# Revit family: Flooring_Entrance-Flooring_emco_DIPLOMAT-Premium
name_source: partatom
category: Furniture Systems
revit_build: Autodesk Revit 2018 (Build: 20190510_1515(x64)
units: mm (PartAtom-declared; Revit-internal decimal feet)

## family parameters
Cut with Voids When Loaded = No
Host = Face
OmniClass Number = 23.15.17.11.11
OmniClass Title = Floor Toppings
Part Type = Normal
Room Calculation Point = No
Round Connector Dimension = Use Diameter
Shared = No

## types (99) — shared parameters
Assembly Code = E2010400
Date Updated = 2023/08/22
Default Elevation = 1219 mm
Description = Rollable and hard-wearing original entrance mat with standard insert for supported installation options.
Keynote = 12480.A1
Manufacturer = Emco
Product data url = https://bimobject.com
Profile Material = Emco - Metal - Aluminium
Standard profile clearance approx. (mm) = 5 mm, rubber spacers
URL = https://www.emco-bau.com
Version = 1

## per-type parameters (varying)
| type | Brush strip | Colour fastness to artificial light ISO 105-B02 | Colour fastness to rubbing ISO 105 X12 | Colour fastness to water ISO 105 E01 | EPIMID | Flammability | Height 12 | Height 17 | Height 22 | Large | Normal | Pile material | Profile width (mm) | Scraping edge | Slip resistance | Tread surface | Weight (kg/m2) | z_Height | z_edge_height | z_insert_offset | z_insert_width | z_slot_offest | z_slot_width |
| Large With Care insert 512 PL Care | No | good 5-6 | good 4-5 | good 4-5 | 99836 | Fire classification for the complete mat system Cfl-s1 in accordance with EN 13501 | Yes | No | No | Yes | No | 100% PA 6 (polyamide) | 44 mm | No | R 12 slip resistance as per DIN 51130 | The robust and exceptionally abrasion-resistant Care insert for the effective reduction of fine dirt. | 8.9 | 12 mm  [stored 0.0393701 ft] | 16 mm | 49 mm | 44 mm  [stored 0.144357 ft] | 47 mm | 5 mm  [stored 0.0164042 ft] |
| Large With Care insert 517 PL Care | No | good 5-6 | good 4-5 | good 4-5 | 99838 | Fire classification for the complete mat system Cfl-s1 in accordance with EN 13501 | No | Yes | No | Yes | No | 100% PA 6 (polyamide) | 44 mm | No | R 12 slip resistance as per DIN 51130 | The robust and exceptionally abrasion-resistant Care insert for the effective reduction of fine dirt. | 95 | 17 mm | 20 mm  [stored 0.0656168 ft] | 49 mm | 44 mm  [stored 0.144357 ft] | 47 mm | 5 mm  [stored 0.0164042 ft] |
| Large With Care insert 522 PL Care | No | good 5-6 | good 4-5 | good 4-5 | 99840 | Fire classification for the complete mat system Cfl-s1 in accordance with EN 13501 | No | No | Yes | Yes | No | 100% PA 6 (polyamide) | 44 mm | No | R 12 slip resistance as per DIN 51130 | The robust and exceptionally abrasion-resistant Care insert for the effective reduction of fine dirt. | 10.5 | 22 mm  [stored 0.0721785 ft] | 25 mm  [stored 0.082021 ft] | 49 mm | 44 mm  [stored 0.144357 ft] | 47 mm | 5 mm  [stored 0.0164042 ft] |
| Large With Care insert and brush strip 517 PL Care B | Yes | good 5-6 | good 4-5 | good 4-5 | 104455 | Insert with fire classification Cfl-s1 according to EN 13501. | No | Yes | No | Yes | No | 100% PA 6 (polyamide) | 44 mm | No | - | The robust and exceptionally abrasion-resistant Care insert for the effective reduction of fine dirt. The additional profile increases the cleaning power. | 9.6 | 17 mm | 20 mm  [stored 0.0656168 ft] | 64 mm | 44 mm  [stored 0.144357 ft] | 54 mm | 20 mm  [stored 0.0656168 ft] |
| Large With Care insert and brush strip 522 PL Care B | Yes | good 5-6 | good 4-5 | good 4-5 | 104456 | Insert with fire classification Cfl-s1 according to EN 13501. | No | No | Yes | Yes | No | 100% PA 6 (polyamide) | 44 mm | No | - | The robust and exceptionally abrasion-resistant Care insert for the effective reduction of fine dirt. The additional profile increases the cleaning power. | 10.7 | 22 mm  [stored 0.0721785 ft] | 25 mm  [stored 0.082021 ft] | 64 mm | 44 mm  [stored 0.144357 ft] | 54 mm | 20 mm  [stored 0.0656168 ft] |
| Large With Care insert and scraping edge 512 PL Care K | No | good 5-6 | good 4-5 | good 4-5 | 104450 | Insert with fire classification Cfl-s1 according to EN 13501. | Yes | No | No | Yes | No | 100% PA 6 (polyamide) | 44 mm | Yes | - | The robust and exceptionally abrasion-resistant Care insert for the effective reduction of fine dirt. The additional profile increases the cleaning power. | 9.2 | 12 mm  [stored 0.0393701 ft] | 16 mm | 59 mm | 44 mm  [stored 0.144357 ft] | 52 mm | 15 mm  [stored 0.0492126 ft] |
| Large With Care insert and scraping edge 517 PL Care K | No | good 5-6 | good 4-5 | good 4-5 | 104451 | Insert with fire classification Cfl-s1 according to EN 13501. | No | Yes | No | Yes | No | 100% PA 6 (polyamide) | 44 mm | Yes | - | The robust and exceptionally abrasion-resistant Care insert for the effective reduction of fine dirt. The additional profile increases the cleaning power. | 13.5 | 17 mm | 20 mm  [stored 0.0656168 ft] | 59 mm | 44 mm  [stored 0.144357 ft] | 52 mm | 15 mm  [stored 0.0492126 ft] |
| Large With Care insert and scraping edge 522 PL Care K | No | good 5-6 | good 4-5 | good 4-5 | 104452 | Insert with fire classification Cfl-s1 according to EN 13501. | No | No | Yes | Yes | No | 100% PA 6 (polyamide) | 44 mm | Yes | - | The robust and exceptionally abrasion-resistant Care insert for the effective reduction of fine dirt. The additional profile increases the cleaning power. | 12 | 22 mm  [stored 0.0721785 ft] | 25 mm  [stored 0.082021 ft] | 59 mm | 44 mm  [stored 0.144357 ft] | 52 mm | 15 mm  [stored 0.0492126 ft] |
| Large With Conform insert 512 PL Conform | No | - | - | - | 99859 | Fire classification for the complete mat system Cfl-s1 in accordance with EN 13501 | Yes | No | No | Yes | No | 100% PA 6 (polyamide) | 44 mm | No | R 12 slip resistance as per DIN 51130 | The Conform insert made of recycled materials is the perfect complement to wooden surroundings and can be used in a whole host of environments. | 9.1 | 12 mm  [stored 0.0393701 ft] | 16 mm | 49 mm | 44 mm  [stored 0.144357 ft] | 47 mm | 5 mm  [stored 0.0164042 ft] |
| Large With Conform insert 517 PL Conform | No | - | - | - | 99863 | Fire classification for the complete mat system Cfl-s1 in accordance with EN 13501 | No | Yes | No | Yes | No | 100% PA 6 (polyamide) | 44 mm | No | R 12 slip resistance as per DIN 51130 | The Conform insert made of recycled materials is the perfect complement to wooden surroundings and can be used in a whole host of environments. | 9.6 | 17 mm | 20 mm  [stored 0.0656168 ft] | 49 mm | 44 mm  [stored 0.144357 ft] | 47 mm | 5 mm  [stored 0.0164042 ft] |
| Large With Conform insert 522 PL Conform | No | - | - | - | 99867 | Fire classification for the complete mat system Cfl-s1 in accordance with EN 13501 | No | No | Yes | Yes | No | 100% PA 6 (polyamide) | 44 mm | No | R 12 slip resistance as per DIN 51130 | The Conform insert made of recycled materials is the perfect complement to wooden surroundings and can be used in a whole host of environments. | 10.6 | 22 mm  [stored 0.0721785 ft] | 25 mm  [stored 0.082021 ft] | 49 mm | 44 mm  [stored 0.144357 ft] | 47 mm | 5 mm  [stored 0.0164042 ft] |
| Large With Conform insert and brush strip 517 PL Conform B | Yes | - | - | - | 105730 | Insert with fire classification Cfl-s1 according to EN 13501. | No | Yes | No | Yes | No | 100% PA 6 (polyamide) | 44 mm | No | - | The Conform insert made of recycled materials is the perfect complement to wooden surroundings and can be used in a whole host of environments. The additional profile increases the cleaning power. | 97 | 17 mm | 20 mm  [stored 0.0656168 ft] | 64 mm | 44 mm  [stored 0.144357 ft] | 54 mm | 20 mm  [stored 0.0656168 ft] |
| Large With Conform insert and brush strip 522 PL Conform B | Yes | - | - | - | 105731 | Insert with fire classification Cfl-s1 according to EN 13501. | No | No | Yes | Yes | No | 100% PA 6 (polyamide) | 44 mm | No | - | The Conform insert made of recycled materials is the perfect complement to wooden surroundings and can be used in a whole host of environments. The additional profile increases the cleaning power. | 10.8 | 22 mm  [stored 0.0721785 ft] | 25 mm  [stored 0.082021 ft] | 64 mm | 44 mm  [stored 0.144357 ft] | 54 mm | 20 mm  [stored 0.0656168 ft] |
| Large With Conform insert and scraping edge 512 PL Conform K | No | - | - | - | 105724 | Insert with fire classification Cfl-s1 according to EN 13501. | Yes | No | No | Yes | No | 100% PA 6 (polyamide) | 44 mm | Yes | - | The Conform insert made of recycled materials is the perfect complement to wooden surroundings and can be used in a whole host of environments. The additional profile increases the cleaning power. | 93 | 12 mm  [stored 0.0393701 ft] | 16 mm | 59 mm | 44 mm  [stored 0.144357 ft] | 52 mm | 15 mm  [stored 0.0492126 ft] |
| Large With Conform insert and scraping edge 517 PL Conform K | No | - | - | - | 105725 | Insert with fire classification Cfl-s1 according to EN 13501. | No | Yes | No | Yes | No | 100% PA 6 (polyamide) | 44 mm | Yes | - | The Conform insert made of recycled materials is the perfect complement to wooden surroundings and can be used in a whole host of environments. The additional profile increases the cleaning power. | 10.6 | 17 mm | 20 mm  [stored 0.0656168 ft] | 59 mm | 44 mm  [stored 0.144357 ft] | 52 mm | 15 mm  [stored 0.0492126 ft] |
| Large With Conform insert and scraping edge 522 PL Conform K | No | - | - | - | 105726 | Insert with fire classification Cfl-s1 according to EN 13501. | No | No | Yes | Yes | No | 100% PA 6 (polyamide) | 44 mm | Yes | - | The Conform insert made of recycled materials is the perfect complement to wooden surroundings and can be used in a whole host of environments. The additional profile increases the cleaning power. | 12.2 | 22 mm  [stored 0.0721785 ft] | 25 mm  [stored 0.082021 ft] | 59 mm | 44 mm  [stored 0.144357 ft] | 52 mm | 15 mm  [stored 0.0492126 ft] |
| Large With Innova insert 512 PL Innova | No | good 5-6 | good 4-5 | good 4-5 | 99843 | Fire classification for the complete mat system Cfl-s1 in accordance with EN 13501 | Yes | No | No | Yes | No | 100% PA 6 (polyamide) | 44 mm | No | R 12 slip resistance as per DIN 51130 | The exceptionally flexible Innova insert not only creates a sophisticated impression but also improves room acoustics. | 87 | 12 mm  [stored 0.0393701 ft] | 16 mm | 49 mm | 44 mm  [stored 0.144357 ft] | 47 mm | 5 mm  [stored 0.0164042 ft] |
| Large With Innova insert 517 PL Innova | No | good 5-6 | good 4-5 | good 4-5 | 99845 | Fire classification for the complete mat system Cfl-s1 in accordance with EN 13501 | No | Yes | No | Yes | No | 100% PA 6 (polyamide) | 44 mm | No | R 12 slip resistance as per DIN 51130 | The exceptionally flexible Innova insert not only creates a sophisticated impression but also improves room acoustics. | 93 | 17 mm | 20 mm  [stored 0.0656168 ft] | 49 mm | 44 mm  [stored 0.144357 ft] | 47 mm | 5 mm  [stored 0.0164042 ft] |
| Large With Innova insert 522 PL Innova | No | good 5-6 | good 4-5 | good 4-5 | 99847 | Fire classification for the complete mat system Cfl-s1 in accordance with EN 13501 | No | No | Yes | Yes | No | 100% PA 6 (polyamide) | 44 mm | No | R 12 slip resistance as per DIN 51130 | The exceptionally flexible Innova insert not only creates a sophisticated impression but also improves room acoustics. | 10.2 | 22 mm  [stored 0.0721785 ft] | 25 mm  [stored 0.082021 ft] | 49 mm | 44 mm  [stored 0.144357 ft] | 47 mm | 5 mm  [stored 0.0164042 ft] |
| Large With Innova insert and brush strip 517 PL Innova B | Yes | good 5-6 | good 4-5 | good 4-5 | 105740 | Insert with fire classification Cfl-s1 according to EN 13501. | No | Yes | No | Yes | No | 100% PA 6 (polyamide) | 44 mm | No | - | The exceptionally flexible Innova insert not only creates a sophisticated impression but also improves room acoustics. The additional profile increases the cleaning power. | 9.4 | 17 mm | 20 mm  [stored 0.0656168 ft] | 64 mm | 44 mm  [stored 0.144357 ft] | 54 mm | 20 mm  [stored 0.0656168 ft] |
| Large With Innova insert and brush strip 522 PL Innova B | Yes | good 5-6 | good 4-5 | good 4-5 | 105741 | Insert with fire classification Cfl-s1 according to EN 13501. | No | No | Yes | Yes | No | 100% PA 6 (polyamide) | 44 mm | No | - | The exceptionally flexible Innova insert not only creates a sophisticated impression but also improves room acoustics. The additional profile increases the cleaning power. | 10.5 | 22 mm  [stored 0.0721785 ft] | 25 mm  [stored 0.082021 ft] | 64 mm | 44 mm  [stored 0.144357 ft] | 54 mm | 20 mm  [stored 0.0656168 ft] |
| Large With Innova insert and scraping edge 512 PL Innova K | No | good 5-6 | good 4-5 | good 4-5 | 105737 | Insert with fire classification Cfl-s1 according to EN 13501. | Yes | No | No | Yes | No | 100% PA 6 (polyamide) | 44 mm | Yes | - | The exceptionally flexible Innova insert not only creates a sophisticated impression but also improves room acoustics. The additional profile increases the cleaning power. | 8.9 | 12 mm  [stored 0.0393701 ft] | 16 mm | 59 mm | 44 mm  [stored 0.144357 ft] | 52 mm | 15 mm  [stored 0.0492126 ft] |
| Large With Innova insert and scraping edge 517 PL Innova K | No | good 5-6 | good 4-5 | good 4-5 | 105738 | Insert with fire classification Cfl-s1 according to EN 13501. | No | Yes | No | Yes | No | 100% PA 6 (polyamide) | 44 mm | Yes | - | The exceptionally flexible Innova insert not only creates a sophisticated impression but also improves room acoustics. The additional profile increases the cleaning power. | 10.3 | 17 mm | 20 mm  [stored 0.0656168 ft] | 59 mm | 44 mm  [stored 0.144357 ft] | 52 mm | 15 mm  [stored 0.0492126 ft] |
| Large With Innova insert and scraping edge 522 PL Innova K | No | good 5-6 | good 4-5 | good 4-5 | 105739 | Insert with fire classification Cfl-s1 according to EN 13501. | No | No | Yes | Yes | No | 100% PA 6 (polyamide) | 44 mm | Yes | - | The exceptionally flexible Innova insert not only creates a sophisticated impression but also improves room acoustics. The additional profile increases the cleaning power. | 119 | 22 mm  [stored 0.0721785 ft] | 25 mm  [stored 0.082021 ft] | 59 mm | 44 mm  [stored 0.144357 ft] | 52 mm | 15 mm  [stored 0.0492126 ft] |
| Large With Maximus Image insert 512 PL Maximus Image | No | good 5-6 | good 5 | good 5 | 100670 | Fire classification for the complete mat system Bfl-s1 in accordance with EN 13501 | Yes | No | No | Yes | No | 100% PA 6.6 (polyamide) | 44 mm | No | R 12 slip resistance as per DIN 51130 | The Maximus Image insert is suitable for single-colour printing in a personally chosen colour. | 8.9 | 12 mm  [stored 0.0393701 ft] | 16 mm | 49 mm | 44 mm  [stored 0.144357 ft] | 47 mm | 5 mm  [stored 0.0164042 ft] |
| Large With Maximus Image insert 512 PL Maximus Image + Design | No | good 5-6 | good 5 | good 5 | 100669 | Fire classification for the complete mat system Bfl-s1 in accordance with EN 13501 | Yes | No | No | Yes | No | 100% PA 6.6 (polyamide) | 44 mm | No | R 12 slip resistance as per DIN 51130 | The Maximus Image insert is suitable for single-colour printing of logos and lettering. | 8.9 | 12 mm  [stored 0.0393701 ft] | 16 mm | 49 mm | 44 mm  [stored 0.144357 ft] | 47 mm | 5 mm  [stored 0.0164042 ft] |
| Large With Maximus Image insert 517 PL Maximus Image | No | good 5-6 | good 5 | good 5 | 100671 | Fire classification for the complete mat system Bfl-s1 in accordance with EN 13501 | No | Yes | No | Yes | No | 100% PA 6.6 (polyamide) | 44 mm | No | R 12 slip resistance as per DIN 51130 | The Maximus Image insert is suitable for single-colour printing in a personally chosen colour. | 95 | 17 mm | 20 mm  [stored 0.0656168 ft] | 49 mm | 44 mm  [stored 0.144357 ft] | 47 mm | 5 mm  [stored 0.0164042 ft] |
| Large With Maximus Image insert 517 PL Maximus Image + Design | No | good 5-6 | good 5 | good 5 | 100668 | Fire classification for the complete mat system Bfl-s1 in accordance with EN 13501 | No | Yes | No | Yes | No | 100% PA 6.6 (polyamide) | 44 mm | No | R 12 slip resistance as per DIN 51130 | The Maximus Image insert is suitable for single-colour printing of logos and lettering. | 95 | 17 mm | 20 mm  [stored 0.0656168 ft] | 49 mm | 44 mm  [stored 0.144357 ft] | 47 mm | 5 mm  [stored 0.0164042 ft] |
| Large With Maximus Image insert 522 PL Maximus Image | No | good 5-6 | good 5 | good 5 | 100672 | Fire classification for the complete mat system Bfl-s1 in accordance with EN 13501 | No | No | Yes | Yes | No | 100% PA 6.6 (polyamide) | 44 mm | No | R 12 slip resistance as per DIN 51130 | The Maximus Image insert is suitable for single-colour printing in a personally chosen colour. | 0 | 22 mm  [stored 0.0721785 ft] | 25 mm  [stored 0.082021 ft] | 49 mm | 44 mm  [stored 0.144357 ft] | 47 mm | 5 mm  [stored 0.0164042 ft] |
| Large With Maximus Image insert 522 PL Maximus Image + Design | No | good 5-6 | good 5 | good 5 | 100665 | Fire classification for the complete mat system Bfl-s1 in accordance with EN 13501 | No | No | Yes | Yes | No | 100% PA 6.6 (polyamide) | 44 mm | No | R 12 slip resistance as per DIN 51130 | The Maximus Image insert is suitable for single-colour printing of logos and lettering. | 0 | 22 mm  [stored 0.0721785 ft] | 25 mm  [stored 0.082021 ft] | 49 mm | 44 mm  [stored 0.144357 ft] | 47 mm | 5 mm  [stored 0.0164042 ft] |
| Large With Maximus Image insert and brush strip 517 PL Maximus Image B | Yes | - | - | - | 104462 | Insert with fire classification Bfl-s1 according to EN 13501. | No | Yes | No | Yes | No | 100% PA 6.6 (polyamide) | 44 mm | No | - | The Maximus Image insert is suitable for single-colour printing in a personally chosen colour. The additional profile increases the cleaning effect. | 10 | 17 mm | 20 mm  [stored 0.0656168 ft] | 64 mm | 44 mm  [stored 0.144357 ft] | 54 mm | 20 mm  [stored 0.0656168 ft] |
| Large With Maximus Image insert and brush strip 522 PL Maximus Image B | Yes | - | - | - | 104463 | Insert with fire classification Bfl-s1 according to EN 13501. | No | No | Yes | Yes | No | 100% PA 6.6 (polyamide) | 44 mm | No | - | The Maximus Image insert is suitable for single-colour printing in a personally chosen colour. The additional profile increases the cleaning effect. | 10.7 | 22 mm  [stored 0.0721785 ft] | 25 mm  [stored 0.082021 ft] | 64 mm | 44 mm  [stored 0.144357 ft] | 54 mm | 20 mm  [stored 0.0656168 ft] |
| Large With Maximus Image insert and scraping edge 512 PL Maximus Image K | No | - | - | - | 105716 | Insert with fire classification Bfl-s1 according to EN 13501. | Yes | No | No | Yes | No | 100% PA 6.6 (polyamide) | 44 mm | Yes | - | The Maximus Image insert is suitable for single-colour printing in a personally chosen colour. The additional profile increases the cleaning effect. | 9.2 | 12 mm  [stored 0.0393701 ft] | 16 mm | 59 mm | 44 mm  [stored 0.144357 ft] | 52 mm | 15 mm  [stored 0.0492126 ft] |
| Large With Maximus Image insert and scraping edge 517 PL Maximus Image K | No | - | - | - | 105718 | Insert with fire classification Bfl-s1 according to EN 13501. | No | Yes | No | Yes | No | 100% PA 6.6 (polyamide) | 44 mm | Yes | - | The Maximus Image insert is suitable for single-colour printing in a personally chosen colour. The additional profile increases the cleaning effect. | 10.5 | 17 mm | 20 mm  [stored 0.0656168 ft] | 59 mm | 44 mm  [stored 0.144357 ft] | 52 mm | 15 mm  [stored 0.0492126 ft] |
| Large With Maximus Image insert and scraping edge 522 PL Maximus Image K | No | - | - | - | 105720 | Insert with fire classification Bfl-s1 according to EN 13501. | No | No | Yes | Yes | No | 100% PA 6.6 (polyamide) | 44 mm | Yes | - | The Maximus Image insert is suitable for single-colour printing in a personally chosen colour. The additional profile increases the cleaning effect. | 121 | 22 mm  [stored 0.0721785 ft] | 25 mm  [stored 0.082021 ft] | 59 mm | 44 mm  [stored 0.144357 ft] | 52 mm | 15 mm  [stored 0.0492126 ft] |
| Large With MAXIMUS insert 512 PL Maximus | No | good 5-6 | good 5 | good 5 | 99831 | Fire classification for the complete mat system Bfl-s1 in accordance with EN 13501 | Yes | No | No | Yes | No | 100% PA 6.6 (polyamide) | 44 mm | No | R 12 slip resistance as per DIN 51130 | The stylish Maximus insert stands out from the crowd with its premium-quality tufted velour and high-end design. | 8.9 | 12 mm  [stored 0.0393701 ft] | 16 mm | 49 mm | 44 mm  [stored 0.144357 ft] | 47 mm | 5 mm  [stored 0.0164042 ft] |
| Large With MAXIMUS insert 517 PL Maximus | No | good 5-6 | good 5 | good 5 | 99832 | Fire classification for the complete mat system Bfl-s1 in accordance with EN 13501 | No | Yes | No | Yes | No | 100% PA 6.6 (polyamide) | 44 mm | No | R 12 slip resistance as per DIN 51130 | The stylish Maximus insert stands out from the crowd with its premium-quality tufted velour and high-end design. | 95 | 17 mm | 20 mm  [stored 0.0656168 ft] | 49 mm | 44 mm  [stored 0.144357 ft] | 47 mm | 5 mm  [stored 0.0164042 ft] |
| Large With MAXIMUS insert 522 PL Maximus | No | good 5-6 | good 5 | good 5 | 99833 | Fire classification for the complete mat system Bfl-s1 in accordance with EN 13501 | No | No | Yes | Yes | No | 100% PA 6.6 (polyamide) | 44 mm | No | R 12 slip resistance as per DIN 51130 | The stylish Maximus insert stands out from the crowd with its premium-quality tufted velour and high-end design. | 0 | 22 mm  [stored 0.0721785 ft] | 25 mm  [stored 0.082021 ft] | 49 mm | 44 mm  [stored 0.144357 ft] | 47 mm | 5 mm  [stored 0.0164042 ft] |
| Large With Maximus insert and brush strip 517 PL Maximus B | Yes | - | - | - | 104461 | Insert with fire classification Bfl-s1 according to EN 13501. | No | Yes | No | Yes | No | 100% PA 6.6 (polyamide) | 44 mm | No | - | The stylish Maximus insert stands out from the crowd with its premium-quality tufted velour and high-end design. The additional profile increases the cleaning power. | 10 | 17 mm | 20 mm  [stored 0.0656168 ft] | 64 mm | 44 mm  [stored 0.144357 ft] | 54 mm | 20 mm  [stored 0.0656168 ft] |
| Large With Maximus insert and brush strip 522 PL Maximus B | Yes | - | - | - | 104464 | Insert with fire classification Bfl-s1 according to EN 13501. | No | No | Yes | Yes | No | 100% PA 6.6 (polyamide) | 44 mm | No | - | The stylish Maximus insert stands out from the crowd with its premium-quality tufted velour and high-end design. The additional profile increases the cleaning power. | 10.7 | 22 mm  [stored 0.0721785 ft] | 25 mm  [stored 0.082021 ft] | 64 mm | 44 mm  [stored 0.144357 ft] | 54 mm | 20 mm  [stored 0.0656168 ft] |
| Large With Maximus insert and scraping edge 512 PL Maximus K | No | - | - | - | 105717 | Insert with fire classification Bfl-s1 according to EN 13501. | Yes | No | No | Yes | No | 100% PA 6.6 (polyamide) | 44 mm | Yes | - | The stylish Maximus insert stands out from the crowd with its premium-quality tufted velour and high-end design. The additional profile increases the cleaning power. | 9.2 | 12 mm  [stored 0.0393701 ft] | 16 mm | 59 mm | 44 mm  [stored 0.144357 ft] | 52 mm | 15 mm  [stored 0.0492126 ft] |
| Large With Maximus insert and scraping edge 517 PL Maximus K | No | - | - | - | 105719 | Insert with fire classification Bfl-s1 according to EN 13501. | No | Yes | No | Yes | No | 100% PA 6.6 (polyamide) | 44 mm | Yes | - | The stylish Maximus insert stands out from the crowd with its premium-quality tufted velour and high-end design. The additional profile increases the cleaning power. | 10.5 | 17 mm | 20 mm  [stored 0.0656168 ft] | 59 mm | 44 mm  [stored 0.144357 ft] | 52 mm | 15 mm  [stored 0.0492126 ft] |
| Large With Maximus insert and scraping edge 522 PL Maximus K | No | - | - | - | 105721 | Insert with fire classification Bfl-s1 according to EN 13501. | No | No | Yes | Yes | No | 100% PA 6.6 (polyamide) | 44 mm | Yes | - | The stylish Maximus insert stands out from the crowd with its premium-quality tufted velour and high-end design. The additional profile increases the cleaning power. | 121 | 22 mm  [stored 0.0721785 ft] | 25 mm  [stored 0.082021 ft] | 59 mm | 44 mm  [stored 0.144357 ft] | 52 mm | 15 mm  [stored 0.0492126 ft] |
| Large With Outdoor insert 512 PL Outdoor | No | excellent 7 | good 4-5 | good 4-5 | 99860 | Fire classification for the complete mat system Cfl-s1 in accordance with EN 13501 | Yes | No | No | Yes | No | 100% PA 6 (polyamide) | 44 mm | No | R 11 slip resistance as per DIN 51130 | The weather-resistant Outdoor insert for noticeably thorough removal of coarse dirt. | 84 | 12 mm  [stored 0.0393701 ft] | 16 mm | 49 mm | 44 mm  [stored 0.144357 ft] | 47 mm | 5 mm  [stored 0.0164042 ft] |
| Large With Outdoor insert 517 PL Outdoor | No | excellent 7 | good 4-5 | good 4-5 | 99864 | Fire classification for the complete mat system Cfl-s1 in accordance with EN 13501 | No | Yes | No | Yes | No | 100% PA 6 (polyamide) | 44 mm | No | R 11 slip resistance as per DIN 51130 | The weather-resistant Outdoor insert for noticeably thorough removal of coarse dirt. | 8.9 | 17 mm | 20 mm  [stored 0.0656168 ft] | 49 mm | 44 mm  [stored 0.144357 ft] | 47 mm | 5 mm  [stored 0.0164042 ft] |
| Large With Outdoor insert 522 PL Outdoor | No | excellent 7 | good 4-5 | good 4-5 | 99868 | Fire classification for the complete mat system Cfl-s1 in accordance with EN 13501 | No | No | Yes | Yes | No | 100% PA 6 (polyamide) | 44 mm | No | R 11 slip resistance as per DIN 51130 | The weather-resistant Outdoor insert for noticeably thorough removal of coarse dirt. | 9.9 | 22 mm  [stored 0.0721785 ft] | 25 mm  [stored 0.082021 ft] | 49 mm | 44 mm  [stored 0.144357 ft] | 47 mm | 5 mm  [stored 0.0164042 ft] |
| Large With Outdoor insert and brush strip 517 PL Outdoor B | Yes | - | - | - | 105760 | Insert with fire classification Cfl-s1 according to EN 13501. | No | Yes | No | Yes | No | 100% PA 6 (polyamide) | 44 mm | No | - | The weather-resistant Outdoor insert for noticeably thorough removal of coarse dirt. The additional profile increases the cleaning power. | 9.2 | 17 mm | 20 mm  [stored 0.0656168 ft] | 64 mm | 44 mm  [stored 0.144357 ft] | 54 mm | 20 mm  [stored 0.0656168 ft] |
| Large With Outdoor insert and brush strip 522 PL Outdoor B | Yes | - | - | - | 105761 | Insert with fire classification Cfl-s1 according to EN 13501. | No | No | Yes | Yes | No | 100% PA 6 (polyamide) | 44 mm | No | - | The weather-resistant Outdoor insert for noticeably thorough removal of coarse dirt. The additional profile increases the cleaning power. | 10.3 | 22 mm  [stored 0.0721785 ft] | 25 mm  [stored 0.082021 ft] | 64 mm | 44 mm  [stored 0.144357 ft] | 54 mm | 20 mm  [stored 0.0656168 ft] |
| Large With Outdoor insert and scraping edge 512 PL Outdoor K | No | - | - | - | 105757 | Insert with fire classification Cfl-s1 according to EN 13501. | Yes | No | No | Yes | No | 100% PA 6 (polyamide) | 44 mm | Yes | - | The weather-resistant Outdoor insert for noticeably thorough removal of coarse dirt. The additional profile increases the cleaning power. | 87 | 12 mm  [stored 0.0393701 ft] | 16 mm | 59 mm | 44 mm  [stored 0.144357 ft] | 52 mm | 15 mm  [stored 0.0492126 ft] |
| Large With Outdoor insert and scraping edge 517 PL Outdoor K | No | - | - | - | 105758 | Insert with fire classification Cfl-s1 according to EN 13501. | No | Yes | No | Yes | No | 100% PA 6 (polyamide) | 44 mm | Yes | - | The weather-resistant Outdoor insert for noticeably thorough removal of coarse dirt. The additional profile increases the cleaning power. | 10 | 17 mm | 20 mm  [stored 0.0656168 ft] | 59 mm | 44 mm  [stored 0.144357 ft] | 52 mm | 15 mm  [stored 0.0492126 ft] |
| Large With Outdoor insert and scraping edge 522 PL Outdoor K | No | - | - | - | 105759 | Insert with fire classification Cfl-s1 according to EN 13501. | No | No | Yes | Yes | No | 100% PA 6 (polyamide) | 44 mm | Yes | - | The weather-resistant Outdoor insert for noticeably thorough removal of coarse dirt. The additional profile increases the cleaning power. | 11.6 | 22 mm  [stored 0.0721785 ft] | 25 mm  [stored 0.082021 ft] | 59 mm | 44 mm  [stored 0.144357 ft] | 52 mm | 15 mm  [stored 0.0492126 ft] |
| With Care insert 512 P Care | No | good 5-6 | good 4-5 | good 4-5 | 99835 | Fire classification for the complete mat system Cfl-s1 in accordance with EN 13501 | Yes | No | No | No | Yes | 100% PA 6 (polyamide) | 27.5 mm | No | R 12 slip resistance as per DIN 51130 | The robust and exceptionally abrasion-resistant Care insert for the effective reduction of fine dirt. | 87 | 12 mm  [stored 0.0393701 ft] | 16 mm | 33 mm | 28 mm | 30 mm  [stored 0.0984252 ft] | 5 mm  [stored 0.0164042 ft] |
| With Care insert 517 P Care | No | good 5-6 | good 4-5 | good 4-5 | 99837 | Fire classification for the complete mat system Cfl-s1 in accordance with EN 13501 | No | Yes | No | No | Yes | 100% PA 6 (polyamide) | 27.5 mm | No | R 12 slip resistance as per DIN 51130 | The robust and exceptionally abrasion-resistant Care insert for the effective reduction of fine dirt. | 94 | 17 mm | 20 mm  [stored 0.0656168 ft] | 33 mm | 28 mm | 30 mm  [stored 0.0984252 ft] | 5 mm  [stored 0.0164042 ft] |
| With Care insert 522 P Care | No | good 5-6 | good 4-5 | good 4-5 | 99839 | Fire classification for the complete mat system Cfl-s1 in accordance with EN 13501 | No | No | Yes | No | Yes | 100% PA 6 (polyamide) | 27.5 mm | No | R 12 slip resistance as per DIN 51130 | The robust and exceptionally abrasion-resistant Care insert for the effective reduction of fine dirt. | 10.5 | 22 mm  [stored 0.0721785 ft] | 25 mm  [stored 0.082021 ft] | 33 mm | 28 mm | 30 mm  [stored 0.0984252 ft] | 5 mm  [stored 0.0164042 ft] |
| With Care insert and brush strip 517 P Care B | Yes | good 5-6 | good 4-5 | good 4-5 | 104453 | Insert with fire classification Cfl-s1 according to EN 13501. | No | Yes | No | No | Yes | 100% PA 6 (polyamide) | 27.5 mm | No | - | The robust and exceptionally abrasion-resistant Care insert for the effective reduction of fine dirt. The additional profile increases the cleaning power. | 95 | 17 mm | 20 mm  [stored 0.0656168 ft] | 47 mm | 28 mm | 37 mm | 20 mm  [stored 0.0656168 ft] |
| With Care insert and brush strip 522 P Care B | Yes | good 5-6 | good 4-5 | good 4-5 | 104454 | Insert with fire classification Cfl-s1 according to EN 13501. | No | No | Yes | No | Yes | 100% PA 6 (polyamide) | 27.5 mm | No | - | The robust and exceptionally abrasion-resistant Care insert for the effective reduction of fine dirt. The additional profile increases the cleaning power. | 10.7 | 22 mm  [stored 0.0721785 ft] | 25 mm  [stored 0.082021 ft] | 47 mm | 28 mm | 37 mm | 20 mm  [stored 0.0656168 ft] |
| With Care insert and scraping edge 512 P Care K | No | good 5-6 | good 4-5 | good 4-5 | 103190 | Insert with fire classification Cfl-s1 according to EN 13501. | Yes | No | No | No | Yes | 100% PA 6 (polyamide) | 27.5 mm | Yes | - | The robust and exceptionally abrasion-resistant Care insert for the effective reduction of fine dirt. The additional profile increases the cleaning power. | 8.9 | 12 mm  [stored 0.0393701 ft] | 16 mm | 43 mm | 28 mm | 35 mm | 15 mm  [stored 0.0492126 ft] |
| With Care insert and scraping edge 517 P Care K | No | good 5-6 | good 4-5 | good 4-5 | 104448 | Insert with fire classification Cfl-s1 according to EN 13501. | No | Yes | No | No | Yes | 100% PA 6 (polyamide) | 27.5 mm | Yes | - | The robust and exceptionally abrasion-resistant Care insert for the effective reduction of fine dirt. The additional profile increases the cleaning power. | 10.3 | 17 mm | 20 mm  [stored 0.0656168 ft] | 43 mm | 28 mm | 35 mm | 15 mm  [stored 0.0492126 ft] |
| With Care insert and scraping edge 522 P Care K | No | good 5-6 | good 4-5 | good 4-5 | 104449 | Insert with fire classification Cfl-s1 according to EN 13501. | No | No | Yes | No | Yes | 100% PA 6 (polyamide) | 27.5 mm | Yes | - | The robust and exceptionally abrasion-resistant Care insert for the effective reduction of fine dirt. The additional profile increases the cleaning power. | 121 | 22 mm  [stored 0.0721785 ft] | 25 mm  [stored 0.082021 ft] | 43 mm | 28 mm | 35 mm | 15 mm  [stored 0.0492126 ft] |
| With Conform insert 512 P Conform | No | - | - | - | 99857 | Fire classification for the complete mat system Cfl-s1 in accordance with EN 13501 | Yes | No | No | No | Yes | 100% PA 6 (polyamide) | 27.5 mm | No | R 12 slip resistance as per DIN 51130 | The Conform insert made of recycled materials is the perfect complement to wooden surroundings and can be used in a whole host of environments. | 88 | 12 mm  [stored 0.0393701 ft] | 16 mm | 33 mm | 28 mm | 30 mm  [stored 0.0984252 ft] | 5 mm  [stored 0.0164042 ft] |
| With Conform insert 517 P Conform | No | - | - | - | 99861 | Fire classification for the complete mat system Cfl-s1 in accordance with EN 13501 | No | Yes | No | No | Yes | 100% PA 6 (polyamide) | 27.5 mm | No | R 12 slip resistance as per DIN 51130 | The Conform insert made of recycled materials is the perfect complement to wooden surroundings and can be used in a whole host of environments. | 95 | 17 mm | 20 mm  [stored 0.0656168 ft] | 33 mm | 28 mm | 30 mm  [stored 0.0984252 ft] | 5 mm  [stored 0.0164042 ft] |
| With Conform insert 522 P Conform | No | - | - | - | 99865 | Fire classification for the complete mat system Cfl-s1 in accordance with EN 13501 | No | No | Yes | No | Yes | 100% PA 6 (polyamide) | 27.5 mm | No | R 12 slip resistance as per DIN 51130 | The Conform insert made of recycled materials is the perfect complement to wooden surroundings and can be used in a whole host of environments. | 10.7 | 22 mm  [stored 0.0721785 ft] | 25 mm  [stored 0.082021 ft] | 33 mm | 28 mm | 30 mm  [stored 0.0984252 ft] | 5 mm  [stored 0.0164042 ft] |
| With Conform insert and brush strip 517 P Conform B | Yes | - | - | - | 105728 | Insert with fire classification Cfl-s1 according to EN 13501. | No | Yes | No | No | Yes | 100% PA 6 (polyamide) | 27.5 mm | No | - | The Conform insert made of recycled materials is the perfect complement to wooden surroundings and can be used in a whole host of environments. The additional profile increases the cleaning power. | 9.6 | 17 mm | 20 mm  [stored 0.0656168 ft] | 47 mm | 28 mm | 37 mm | 20 mm  [stored 0.0656168 ft] |
| With Conform insert and brush strip 522 P Conform B | Yes | - | - | - | 105729 | Insert with fire classification Cfl-s1 according to EN 13501. | No | No | Yes | No | Yes | 100% PA 6 (polyamide) | 27.5 mm | No | - | The Conform insert made of recycled materials is the perfect complement to wooden surroundings and can be used in a whole host of environments. The additional profile increases the cleaning power. | 10.8 | 22 mm  [stored 0.0721785 ft] | 25 mm  [stored 0.082021 ft] | 47 mm | 28 mm | 37 mm | 20 mm  [stored 0.0656168 ft] |
| With Conform insert and scraping edge 512 P Conform K | No | - | - | - | 105727 | Insert with fire classification Cfl-s1 according to EN 13501. | Yes | No | No | No | Yes | 100% PA 6 (polyamide) | 27.5 mm | Yes | - | The Conform insert made of recycled materials is the perfect complement to wooden surroundings and can be used in a whole host of environments. The additional profile increases the cleaning power. | 90 | 12 mm  [stored 0.0393701 ft] | 16 mm | 43 mm | 28 mm | 35 mm | 15 mm  [stored 0.0492126 ft] |
| With Conform insert and scraping edge 517 P Conform K | No | - | - | - | 105722 | Insert with fire classification Cfl-s1 according to EN 13501. | No | Yes | No | No | Yes | 100% PA 6 (polyamide) | 27.5 mm | Yes | - | The Conform insert made of recycled materials is the perfect complement to wooden surroundings and can be used in a whole host of environments. The additional profile increases the cleaning power. | 11.2 | 17 mm | 20 mm  [stored 0.0656168 ft] | 43 mm | 28 mm | 35 mm | 15 mm  [stored 0.0492126 ft] |
| With Conform insert and scraping edge 522 P Conform K | No | - | - | - | 105723 | Insert with fire classification Cfl-s1 according to EN 13501. | No | No | Yes | No | Yes | 100% PA 6 (polyamide) | 27.5 mm | Yes | - | The Conform insert made of recycled materials is the perfect complement to wooden surroundings and can be used in a whole host of environments. The additional profile increases the cleaning power. | 12.2 | 22 mm  [stored 0.0721785 ft] | 25 mm  [stored 0.082021 ft] | 43 mm | 28 mm | 35 mm | 15 mm  [stored 0.0492126 ft] |
| With Innova insert 512 P Innova | No | good 5-6 | good 4-5 | good 4-5 | 99842 | Fire classification for the complete mat system Cfl-s1 in accordance with EN 13501 | Yes | No | No | No | Yes | 100% PA 6 (polyamide) | 27.5 mm | No | R 12 slip resistance as per DIN 51130 | The exceptionally flexible Innova insert not only creates a sophisticated impression but also improves room acoustics. | 86 | 12 mm  [stored 0.0393701 ft] | 16 mm | 33 mm | 28 mm | 30 mm  [stored 0.0984252 ft] | 5 mm  [stored 0.0164042 ft] |
| With Innova insert 517 P Innova | No | good 5-6 | good 4-5 | good 4-5 | 99844 | Fire classification for the complete mat system Cfl-s1 in accordance with EN 13501 | No | Yes | No | No | Yes | 100% PA 6 (polyamide) | 27.5 mm | No | R 12 slip resistance as per DIN 51130 | The exceptionally flexible Innova insert not only creates a sophisticated impression but also improves room acoustics. | 9.4 | 17 mm | 20 mm  [stored 0.0656168 ft] | 33 mm | 28 mm | 30 mm  [stored 0.0984252 ft] | 5 mm  [stored 0.0164042 ft] |
| With Innova insert 522 P Innova | No | good 5-6 | good 4-5 | good 4-5 | 99846 | Fire classification for the complete mat system Cfl-s1 in accordance with EN 13501 | No | No | Yes | No | Yes | 100% PA 6 (polyamide) | 27.5 mm | No | R 12 slip resistance as per DIN 51130 | The exceptionally flexible Innova insert not only creates a sophisticated impression but also improves room acoustics. | 10.5 | 22 mm  [stored 0.0721785 ft] | 25 mm  [stored 0.082021 ft] | 33 mm | 28 mm | 30 mm  [stored 0.0984252 ft] | 5 mm  [stored 0.0164042 ft] |
| With Innova insert and brush strip 517 P Innova B | Yes | good 5-6 | good 4-5 | good 4-5 | 105735 | Insert with fire classification Cfl-s1 according to EN 13501. | No | Yes | No | No | Yes | 100% PA 6 (polyamide) | 27.5 mm | No | - | The exceptionally flexible Innova insert not only creates a sophisticated impression but also improves room acoustics. The additional profile increases the cleaning power. | 9.4 | 17 mm | 20 mm  [stored 0.0656168 ft] | 47 mm | 28 mm | 37 mm | 20 mm  [stored 0.0656168 ft] |
| With Innova insert and brush strip 522 P Innova B | Yes | good 5-6 | good 4-5 | good 4-5 | 105736 | Insert with fire classification Cfl-s1 according to EN 13501. | No | No | Yes | No | Yes | 100% PA 6 (polyamide) | 27.5 mm | No | - | The exceptionally flexible Innova insert not only creates a sophisticated impression but also improves room acoustics. The additional profile increases the cleaning power. | 10.7 | 22 mm  [stored 0.0721785 ft] | 25 mm  [stored 0.082021 ft] | 47 mm | 28 mm | 37 mm | 20 mm  [stored 0.0656168 ft] |
| With Innova insert and scraping edge 512 P Innova K | No | good 5-6 | good 4-5 | good 4-5 | 105732 | Insert with fire classification Cfl-s1 according to EN 13501. | Yes | No | No | No | Yes | 100% PA 6 (polyamide) | 27.5 mm | Yes | - | The exceptionally flexible Innova insert not only creates a sophisticated impression but also improves room acoustics. The additional profile increases the cleaning power. | 8.9 | 12 mm  [stored 0.0393701 ft] | 16 mm | 43 mm | 28 mm | 35 mm | 15 mm  [stored 0.0492126 ft] |
| With Innova insert and scraping edge 517 P Innova K | No | good 5-6 | good 4-5 | good 4-5 | 105733 | Insert with fire classification Cfl-s1 according to EN 13501. | No | Yes | No | No | Yes | 100% PA 6 (polyamide) | 27.5 mm | Yes | - | The exceptionally flexible Innova insert not only creates a sophisticated impression but also improves room acoustics. The additional profile increases the cleaning power. | 10.2 | 17 mm | 20 mm  [stored 0.0656168 ft] | 43 mm | 28 mm | 35 mm | 15 mm  [stored 0.0492126 ft] |
| With Innova insert and scraping edge 522 P Innova K | No | good 5-6 | good 4-5 | good 4-5 | 105734 | Insert with fire classification Cfl-s1 according to EN 13501. | No | No | Yes | No | Yes | 100% PA 6 (polyamide) | 27.5 mm | Yes | - | The exceptionally flexible Innova insert not only creates a sophisticated impression but also improves room acoustics. The additional profile increases the cleaning power. | 121 | 22 mm  [stored 0.0721785 ft] | 25 mm  [stored 0.082021 ft] | 43 mm | 28 mm | 35 mm | 15 mm  [stored 0.0492126 ft] |
| With Maximus Image insert 512 P Maximus Image | No | good 5-6 | good 5 | good 5 | 100667 | Fire classification for the complete mat system Bfl-s1 in accordance with EN 13501 | Yes | No | No | No | Yes | 100% PA 6.6 (polyamide) | 27.5 mm | No | R 12 slip resistance as per DIN 51130 | The Maximus Image insert is suitable for single-colour printing in a personally chosen colour. | 87 | 12 mm  [stored 0.0393701 ft] | 16 mm | 33 mm | 28 mm | 30 mm  [stored 0.0984252 ft] | 5 mm  [stored 0.0164042 ft] |
| With Maximus Image insert 517 P Maximus Image | No | good 5-6 | good 5 | good 5 | 100666 | Fire classification for the complete mat system Bfl-s1 in accordance with EN 13501 | No | Yes | No | No | Yes | 100% PA 6.6 (polyamide) | 27.5 mm | No | R 12 slip resistance as per DIN 51130 | The Maximus Image insert is suitable for single-colour printing in a personally chosen colour. | 9.4 | 17 mm | 20 mm  [stored 0.0656168 ft] | 33 mm | 28 mm | 30 mm  [stored 0.0984252 ft] | 5 mm  [stored 0.0164042 ft] |
| With Maximus Image insert 522 P Maximus Image | No | good 5-6 | good 5 | good 5 | 100664 | Fire classification for the complete mat system Bfl-s1 in accordance with EN 13501 | No | No | Yes | No | Yes | 100% PA 6.6 (polyamide) | 27.5 mm | No | R 12 slip resistance as per DIN 51130 | The Maximus Image insert is suitable for single-colour printing in a personally chosen colour. | 10.5 | 22 mm  [stored 0.0721785 ft] | 25 mm  [stored 0.082021 ft] | 33 mm | 28 mm | 30 mm  [stored 0.0984252 ft] | 5 mm  [stored 0.0164042 ft] |
| With Maximus Image insert and brush strip 517 P Maximus Image B | Yes | - | - | - | 104458 | Insert with fire classification Bfl-s1 according to EN 13501. | No | Yes | No | No | Yes | 100% PA 6.6 (polyamide) | 27.5 mm | No | - | The Maximus Image insert is suitable for single-colour printing in a personally chosen colour. The additional profile increases the cleaning effect. | 95 | 17 mm | 20 mm  [stored 0.0656168 ft] | 47 mm | 28 mm | 37 mm | 20 mm  [stored 0.0656168 ft] |
| With Maximus Image insert and brush strip 522 P Maximus Image B | Yes | - | - | - | 104459 | Insert with fire classification Bfl-s1 according to EN 13501. | No | No | Yes | No | Yes | 100% PA 6.6 (polyamide) | 27.5 mm | No | - | The Maximus Image insert is suitable for single-colour printing in a personally chosen colour. The additional profile increases the cleaning effect. | 10.7 | 22 mm  [stored 0.0721785 ft] | 25 mm  [stored 0.082021 ft] | 47 mm | 28 mm | 37 mm | 20 mm  [stored 0.0656168 ft] |
| With Maximus Image insert and scraping edge 512 P Maximus Image K | No | - | - | - | 105711 | Insert with fire classification Bfl-s1 according to EN 13501. | Yes | No | No | No | Yes | 100% PA 6.6 (polyamide) | 27.5 mm | Yes | - | The Maximus Image insert is suitable for single-colour printing in a personally chosen colour. The additional profile increases the cleaning effect. | 90 | 12 mm  [stored 0.0393701 ft] | 16 mm | 43 mm | 28 mm | 35 mm | 15 mm  [stored 0.0492126 ft] |
| With Maximus Image insert and scraping edge 517 P Maximus Image K | No | - | - | - | 105713 | Insert with fire classification Bfl-s1 according to EN 13501. | No | Yes | No | No | Yes | 100% PA 6.6 (polyamide) | 27.5 mm | Yes | - | The Maximus Image insert is suitable for single-colour printing in a personally chosen colour. The additional profile increases the cleaning effect. | 10.3 | 17 mm | 20 mm  [stored 0.0656168 ft] | 43 mm | 28 mm | 35 mm | 15 mm  [stored 0.0492126 ft] |
| With Maximus Image insert and scraping edge 522 P Maximus Image K | No | - | - | - | 105715 | Insert with fire classification Bfl-s1 according to EN 13501. | No | No | Yes | No | Yes | 100% PA 6.6 (polyamide) | 27.5 mm | Yes | - | The Maximus Image insert is suitable for single-colour printing in a personally chosen colour. The additional profile increases the cleaning effect. | 121 | 22 mm  [stored 0.0721785 ft] | 25 mm  [stored 0.082021 ft] | 43 mm | 28 mm | 35 mm | 15 mm  [stored 0.0492126 ft] |
| With MAXIMUS insert 512 P Maximus | No | good 5-6 | good 5 | good 5 | 99829 | Fire classification for the complete mat system Bfl-s1 in accordance with EN 13501 | Yes | No | No | No | Yes | 100% PA 6.6 (polyamide) | 27.5 mm | No | R 12 slip resistance as per DIN 51130 | The stylish Maximus insert stands out from the crowd with its premium-quality tufted velour and high-end design. | 87 | 12 mm  [stored 0.0393701 ft] | 16 mm | 33 mm | 28 mm | 30 mm  [stored 0.0984252 ft] | 5 mm  [stored 0.0164042 ft] |
| With MAXIMUS insert 517 P Maximus | No | good 5-6 | good 5 | good 5 | 99828 | Fire classification for the complete mat system Bfl-s1 in accordance with EN 13501 | No | Yes | No | No | Yes | 100% PA 6.6 (polyamide) | 27.5 mm | No | R 12 slip resistance as per DIN 51130 | The stylish Maximus insert stands out from the crowd with its premium-quality tufted velour and high-end design. | 9.4 | 17 mm | 20 mm  [stored 0.0656168 ft] | 33 mm | 28 mm | 30 mm  [stored 0.0984252 ft] | 5 mm  [stored 0.0164042 ft] |
| With MAXIMUS insert 522 P Maximus | No | good 5-6 | good 5 | good 5 | 99830 | Fire classification for the complete mat system Bfl-s1 in accordance with EN 13501 | No | No | Yes | No | Yes | 100% PA 6.6 (polyamide) | 27.5 mm | No | R 12 slip resistance as per DIN 51130 | The stylish Maximus insert stands out from the crowd with its premium-quality tufted velour and high-end design. | 10.5 | 22 mm  [stored 0.0721785 ft] | 25 mm  [stored 0.082021 ft] | 33 mm | 28 mm | 30 mm  [stored 0.0984252 ft] | 5 mm  [stored 0.0164042 ft] |
| With Maximus insert and brush strip 517 P Maximus B | Yes | - | - | - | 104457 | Insert with fire classification Bfl-s1 according to EN 13501. | No | Yes | No | No | Yes | 100% PA 6.6 (polyamide) | 27.5 mm | No | - | The stylish Maximus insert stands out from the crowd with its premium-quality tufted velour and high-end design. The additional profile increases the cleaning power. | 95 | 17 mm | 20 mm  [stored 0.0656168 ft] | 47 mm | 28 mm | 37 mm | 20 mm  [stored 0.0656168 ft] |
| With Maximus insert and brush strip 522 P Maximus B | Yes | - | - | - | 104460 | Insert with fire classification Bfl-s1 according to EN 13501. | No | No | Yes | No | Yes | 100% PA 6.6 (polyamide) | 27.5 mm | No | - | The stylish Maximus insert stands out from the crowd with its premium-quality tufted velour and high-end design. The additional profile increases the cleaning power. | 10.7 | 22 mm  [stored 0.0721785 ft] | 25 mm  [stored 0.082021 ft] | 47 mm | 28 mm | 37 mm | 20 mm  [stored 0.0656168 ft] |
| With Maximus insert and scraping edge 512 P Maximus K | No | - | - | - | 105710 | Insert with fire classification Bfl-s1 according to EN 13501. | Yes | No | No | No | Yes | 100% PA 6.6 (polyamide) | 27.5 mm | Yes | - | The stylish Maximus insert stands out from the crowd with its premium-quality tufted velour and high-end design. The additional profile increases the cleaning power. | 90 | 12 mm  [stored 0.0393701 ft] | 16 mm | 43 mm | 28 mm | 35 mm | 15 mm  [stored 0.0492126 ft] |
| With Maximus insert and scraping edge 517 P Maximus K | No | - | - | - | 105712 | Insert with fire classification Bfl-s1 according to EN 13501. | No | Yes | No | No | Yes | 100% PA 6.6 (polyamide) | 27.5 mm | Yes | - | The stylish Maximus insert stands out from the crowd with its premium-quality tufted velour and high-end design. The additional profile increases the cleaning power. | 10.3 | 17 mm | 20 mm  [stored 0.0656168 ft] | 43 mm | 28 mm | 35 mm | 15 mm  [stored 0.0492126 ft] |
| With Maximus insert and scraping edge 522 P Maximus K | No | - | - | - | 105714 | Insert with fire classification Bfl-s1 according to EN 13501. | No | No | Yes | No | Yes | 100% PA 6.6 (polyamide) | 27.5 mm | Yes | - | The stylish Maximus insert stands out from the crowd with its premium-quality tufted velour and high-end design. The additional profile increases the cleaning power. | 121 | 22 mm  [stored 0.0721785 ft] | 25 mm  [stored 0.082021 ft] | 43 mm | 28 mm | 35 mm | 15 mm  [stored 0.0492126 ft] |
| With Outdoor insert 512 P Outdoor | No | excellent 7 | good 4-5 | good 4-5 | 99858 | Fire classification for the complete mat system Cfl-s1 in accordance with EN 13501 | Yes | No | No | No | Yes | 100% PA 6 (polyamide) | 27.5 mm | No | R 11 slip resistance as per DIN 51130 | The weather-resistant Outdoor insert for noticeably thorough removal of coarse dirt. | 83 | 12 mm  [stored 0.0393701 ft] | 16 mm | 33 mm | 28 mm | 30 mm  [stored 0.0984252 ft] | 5 mm  [stored 0.0164042 ft] |
| With Outdoor insert 517 P Outdoor | No | excellent 7 | good 4-5 | good 4-5 | 99862 | Fire classification for the complete mat system Cfl-s1 in accordance with EN 13501 | No | Yes | No | No | Yes | 100% PA 6 (polyamide) | 27.5 mm | No | R 11 slip resistance as per DIN 51130 | The weather-resistant Outdoor insert for noticeably thorough removal of coarse dirt. | 9.1 | 17 mm | 20 mm  [stored 0.0656168 ft] | 33 mm | 28 mm | 30 mm  [stored 0.0984252 ft] | 5 mm  [stored 0.0164042 ft] |
| With Outdoor insert 522 P Outdoor | No | excellent 7 | good 4-5 | good 4-5 | 99866 | Fire classification for the complete mat system Cfl-s1 in accordance with EN 13501 | No | No | Yes | No | Yes | 100% PA 6 (polyamide) | 27.5 mm | No | R 11 slip resistance as per DIN 51130 | The weather-resistant Outdoor insert for noticeably thorough removal of coarse dirt. | 10.2 | 22 mm  [stored 0.0721785 ft] | 25 mm  [stored 0.082021 ft] | 33 mm | 28 mm | 30 mm  [stored 0.0984252 ft] | 5 mm  [stored 0.0164042 ft] |
| With Outdoor insert and brush strip 517 P Outdoor B | Yes | - | - | - | 105755 | Insert with fire classification Cfl-s1 according to EN 13501. | No | Yes | No | No | Yes | 100% PA 6 (polyamide) | 27.5 mm | No | - | The weather-resistant Outdoor insert for noticeably thorough removal of coarse dirt. The additional profile increases the cleaning power. | 9.2 | 17 mm | 20 mm  [stored 0.0656168 ft] | 47 mm | 28 mm | 37 mm | 20 mm  [stored 0.0656168 ft] |
| With Outdoor insert and brush strip 522 P Outdoor B | Yes | - | - | - | 105756 | Insert with fire classification Cfl-s1 according to EN 13501. | No | No | Yes | No | Yes | 100% PA 6 (polyamide) | 27.5 mm | No | - | The weather-resistant Outdoor insert for noticeably thorough removal of coarse dirt. The additional profile increases the cleaning power. | 11.3 | 22 mm  [stored 0.0721785 ft] | 25 mm  [stored 0.082021 ft] | 47 mm | 28 mm | 37 mm | 20 mm  [stored 0.0656168 ft] |
| With Outdoor insert and scraping edge 512 P Outdoor K | No | - | - | - | 105752 | Insert with fire classification Cfl-s1 according to EN 13501. | Yes | No | No | No | Yes | 100% PA 6 (polyamide) | 27.5 mm | Yes | - | The weather-resistant Outdoor insert for noticeably thorough removal of coarse dirt. The additional profile increases the cleaning power. | 87 | 12 mm  [stored 0.0393701 ft] | 16 mm | 43 mm | 28 mm | 35 mm | 15 mm  [stored 0.0492126 ft] |
| With Outdoor insert and scraping edge 517 P Outdoor K | No | - | - | - | 105753 | Insert with fire classification Cfl-s1 according to EN 13501. | No | Yes | No | No | Yes | 100% PA 6 (polyamide) | 27.5 mm | Yes | - | The weather-resistant Outdoor insert for noticeably thorough removal of coarse dirt. The additional profile increases the cleaning power. | 10 | 17 mm | 20 mm  [stored 0.0656168 ft] | 43 mm | 28 mm | 35 mm | 15 mm  [stored 0.0492126 ft] |
| With Outdoor insert and scraping edge 522 P Outdoor K | No | - | - | - | 105754 | Insert with fire classification Cfl-s1 according to EN 13501. | No | No | Yes | No | Yes | 100% PA 6 (polyamide) | 27.5 mm | Yes | - | The weather-resistant Outdoor insert for noticeably thorough removal of coarse dirt. The additional profile increases the cleaning power. | 119 | 22 mm  [stored 0.0721785 ft] | 25 mm  [stored 0.082021 ft] | 43 mm | 28 mm | 35 mm | 15 mm  [stored 0.0492126 ft] |

note: column(s) folded — value = type name in every type: Model

note: [stored X ft] marks values corroborated as IEEE doubles in the binary element streams (Revit-internal decimal feet)

## geometry (parser evidence)
native form markers: Sweep x6
no freeform markers — native parametric forms only
